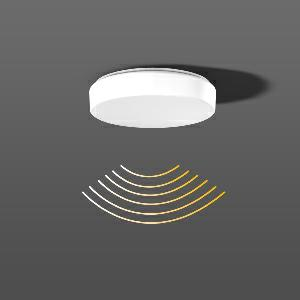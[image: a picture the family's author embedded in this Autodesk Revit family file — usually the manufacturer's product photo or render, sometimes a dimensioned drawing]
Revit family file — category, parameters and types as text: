
# Revit family: flat_polymero_kreis_311620_002_5_19_08ac
name_source: partatom
category: Lighting Fixtures
units: mm (PartAtom-declared; Revit-internal decimal feet)

## family parameters
Cut with Voids When Loaded = No
Host = Face
Light Source = No
Part Type = Normal
Room Calculation Point = No
Round Connector Dimension = Use Diameter
Shared = No

## types (1)
- FLAT POLYMERO KREIS (1 x LED Modul 840, 1500 lm, 4000)
    Apparent Load = 14 VA
    CIE Flux Codes = 40 70 90 80 100
    Color Rendering = 80
    Color Temperature = 4000
    Default Elevation = 1800 mm
    Description = Series: FLAT POLYMERO KREIS
Decorative round surface-mounted luminaire. Base: metal, powder-coated. Diffuser made of non-yellowing plastic (PMMA), opal. Diffuser fastening: patented push system. Suitable for Ceiling mounting, Wall (surface). With integrated HF movement sensor. Functional parameters of the motion detector (ceiling mounting up to 4.0 m or wall mounting up to 2.7 m): HF detector 5.8 GHz ISM frequency band. Sensitivity/Range: 1-8 m in diameter, adjustable from 20-100%. Time control between 10 seconds and 30 minutes, adjustable. Coverage: 120°. Can be used as master luminaire up to 800 W (ohmic load), 500 W (fluorescent lamp, LED) / 400 A, 200 µs. Suitable for outdoor use to a limited extent only, as it is sensitive to all movements. 
Colour: white
Diameter: 300 mm
Height: 80 mm
Lamp: LED
Socket: without socket
Colour temperature: 4000K
Colour rendering index (CRI): 80
System power: 14 W
Rated luminous flux: 1500 lm
Luminous efficiency: 107 lm/W
Control gear: Regulated power supply
Protection class: I
Type of protection: IP 40
    Height = 80 mm  [stored 0.262467 ft]
    Lamp = 1 x LED Modul 840
    Lamp Light Flux = 1500 lm
    Lamp count = 1
    Length = 300 mm
    Lifetime = 50000 h
    Luminous efficacy = 107 lm/W
    Manufacturer = RZB
    ModVariant = No
    Model = 311620.002.5.19
    Mounting Place = Ceiling, Wall
    Mounting Type = Surface mounted
    Number of Poles = 1
    OnlyDefault = Yes
    Power Factor = 1
    Product Name = FLAT POLYMERO KREIS
    Product group = Surface mounted ceiling and wall luminaires
    ProductGroupID = 305
    Protection Class = Protection class I
    Protection Degree = IP 40
    RLX_Detail_Level = 1
    RLX_Emergency_Light_Flux = 0 lm
    RLX_Emergency_Type = 0
    RLX_Emergency_Type_DB = No
    RlxData = <blob elided: 65121 chars, md5=de355dc5>
    Socket = socket
    Standby Power = 0 W
    System Light Flux = 1500 lm
    System Power = 14 W
    Type Comments = Product without accessories
    Type Image = 311599.002.19.jpg
    URL = http://relux.com
    VarID = ---
    Voltage = 230 V
    Voltage Range = 220-240 V
    Weight = 0.00 kg
    Width = 0 mm  [stored 0 ft]

note: [stored X ft] marks values corroborated as IEEE doubles in the binary element streams (Revit-internal decimal feet)

## geometry (parser evidence)
native form markers: Blend x4, Sweep x13
no freeform markers — native parametric forms only
